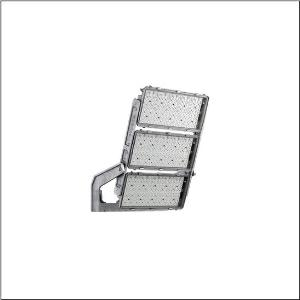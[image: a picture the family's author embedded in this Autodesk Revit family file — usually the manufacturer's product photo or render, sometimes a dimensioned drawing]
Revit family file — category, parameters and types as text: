
# Revit family: floodlight_fl_11_maxi_pro_remote___pl33t_5xa779427f01ba_72f0
name_source: partatom
category: Lighting Fixtures
units: mm (PartAtom-declared; Revit-internal decimal feet)

## family parameters
Cut with Voids When Loaded = No
Host = Face
Light Source = No
Part Type = Normal
Room Calculation Point = No
Round Connector Dimension = Use Diameter
Shared = No

## types (1)
- --- (1 x LED, 132850 lm, 953.7 W, 5000K)
    Apparent Load = 954 VA
    CIE Flux Codes = 25 74 99 100 100
    Color Rendering = 70
    Color Temperature = 5000K
    Default Elevation = 1800 mm
    Description = Floodlight FL 11  maxi  pro Remote floodlight; light control with lens of PMMA; cover panel of toughened safety glass, transparent; light distribution: PL33T, asymmetric direct distribution, LEDcolour temperature: 5000K, rated luminous flux: 132.850lm, colour rendering: CRI > 70, light colour: 750; luminous efficacy: 139lm/W; brightness control: DALI 2 (1 DALI address); with terminal, 8-pole, max. 2.5mm², mains connection: 220..240V/380..400V AC, 50/60Hz, surge voltage resistance: line to ground: 10kV, ECG replaceable separately, no afterglow with DALI off / DMX off command, LED unit replaceable without ESD environment, dustproof LED module, dimming range 10..100%; 954W floodlight with 2x LED unit of diecast aluminium, coated grey; length: 713mm / width: 651mm / height: 338mm; mounting bracket, of diecast aluminium, uncoated, natural, equipment: Longlife, protection rating (complete): IP66; insulation class (complete): insulation class I (protective earthing); certification: CE, ENEC, VDE; ball protection: ball impact resistance with accessories, impact resistance: IK07; only for outdoor installations, rated ambient temperature 10°C, permissible operating ambient temperature: -40..+30°C, permissible storage temperature: -40..+85°C; packaging unit: 1 piece

Light Distribution: PL33T
    Height = 320 mm
    Lamp = 1 x LED
    Lamp Light Flux = 132850 lm
    Lamp Power = 953.7 W
    Lamp count = 1
    Length = 1002 mm
    Luminous efficacy = 139 lm/W
    Manufacturer = Siteco
    ModVariant = No
    Model = 5XA779427F01BA
    Mounting Place = Ceiling
    Mounting Type = Surface mounted
    Number of Poles = 1
    OnlyDefault = Yes
    Power Factor = 1
    Product Name = Floodlight FL 11 maxi pro Remote | PL33T
    Product group = floodlight | ceiling mounted
    ProductGroupID = 303
    Protection Class = Protection class I
    Protection Degree = IP 66
    RLX_Detail_Level = 1
    RLX_Emergency_Light_Flux = 0 lm
    RLX_Emergency_Type = 0
    RLX_Emergency_Type_DB = No
    RlxData = <blob elided: 52485 chars, md5=58e43253>
    Socket = socket
    Standby Power = 0 W
    System Light Flux = 132850 lm
    System Power = 954 W
    Type Comments = factory setting: luminous flux: 100 % | dim-lin: 254 | 665 mA
    Type Image = l_1006784.jpg
    URL = http://relux.com
    VarID = @adj_045593
    Voltage = 0 V
    Weight = 0.00 kg
    Width = 655 mm

## geometry (parser evidence)
native form markers: Blend x4, Sweep x15
no freeform markers — native parametric forms only
